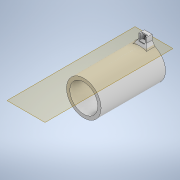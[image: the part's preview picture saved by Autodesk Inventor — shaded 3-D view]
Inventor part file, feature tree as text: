
AUTODESK INVENTOR PART (.ipt)
format: ipt  version: 2021 (Build 250183000, 183)  size: 569,344 bytes
history: native  units: in
note: dims shown in document units (in); Inventor stores cm internally (conversion verified against a paired STEP export)
features: projected_geometry x11, extrude x9, sketch x5, chamfer x3, fillet x2, plane x1, pattern_linear x1
ambient origin geometry x8: Origin, YZ Plane, XZ Plane, XY Plane, X Axis, Y Axis, Z Axis, Center Point
bodies: Solid1 (feature_tree)
feature tree (32):
  extrude  "Extrusion1"  Depth=3.2677in TaperAngle=0.0deg
  plane  "Work Plane1"
  extrude  "Extrusion7"  Depth=3.189in TaperAngle=0.0deg
  extrude  "Extrusion8"  Depth=0.3937in
  extrude  "Extrusion9"  Depth=0.3937in
  extrude  "Extrusion10"  Depth=0.3937in TaperAngle=0.0deg
  extrude  "Extrusion11"  Depth=0.3937in
  extrude  "Extrusion12"  Depth=0.3937in
  pattern_linear  "Rectangular Pattern3"  Spacing1=0.1969in  [1 undecoded]
  extrude  "Extrusion13"  Depth=0.3937in TaperAngle=0.0deg
  chamfer  "Chamfer2"  Distance=1.811in
  chamfer  "Chamfer4"  Distance=0.0394in
  chamfer  "Chamfer5"  Distance=0.0098in
  extrude  "Extrusion14"  Depth=0.0787in
  fillet  "Fillet11"  Radius=0.1181in
  fillet  "Fillet12"  Radius=0.3937in
  sketch  "Sketch2"  dims[d2=1.752in d3=3.2677in d4=0.0in]
  sketch  "Sketch9"  dims[d54=1.4173in d55=3.189in d56=0.0in]
  projected_geometry  "Projected Loop7"
  sketch  "Sketch10"  dims[d57=0.3937in d58=0.2756in]
  projected_geometry  "Projected Loop8"
  projected_geometry  "Projected Loop9"
  projected_geometry  "Projected Loop10"
  projected_geometry  "Projected Loop11"
  projected_geometry  "Projected Loop12"
  projected_geometry  "Projected Loop14"
  projected_geometry  "Projected Loop15"
  sketch  "Sketch16"  dims[d59=0.3937in d60=0.0236in d61=0.0in d62=0.0in d63=0.2047in]
  projected_geometry  "Projected Loop16"
  sketch  "Sketch17"  dims[d64=0.126in d66=0.0295in d67=0.0in d68=0.0591in d69=0.0591in d71=0.1969in d72=0.0in d76=1.1811in d77=0.0in d84=1.811in d85=0.0394in d86=0.0098in d87=0.0in d88=8.2677in d90=0.0787in d92=0.1181in d93=0.3937in d94=0.0in d96=0.0059in d97=0.0185in d98=0.0787in d99=45.0deg d103=0.1575in d104=0.0787in d105=45.0deg d106=0.0098in d107=0.0787in d108=45.0deg d109=0.2756in d110=0.0315in d111=0.0in d116=0.4724in d117=0.3937in d19=0.0197in d20=0.0344in d21=0.0197in d22=0.0344in]
  projected_geometry  "Projected Loop17"
  projected_geometry  "Projected Loop18"
note: 1 required parameter value undecoded (feature->parameter linkage not recoverable at this tier; creation-order binding heuristic only, values carry confidence <= 0.55)
